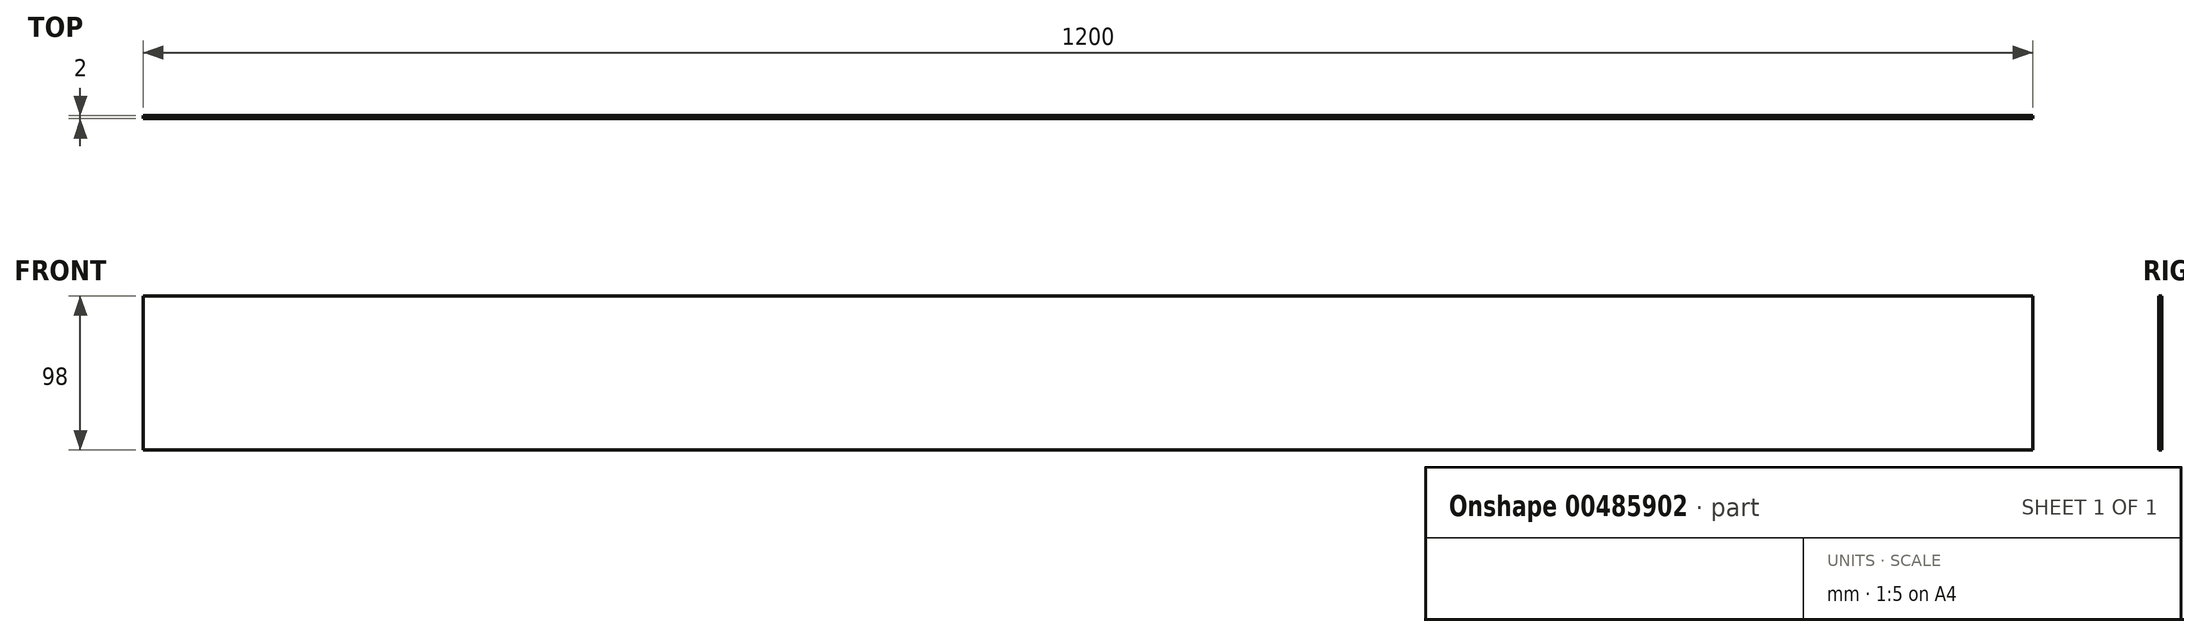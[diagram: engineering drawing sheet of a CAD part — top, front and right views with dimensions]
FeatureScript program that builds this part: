
annotation { "Feature Type Name" : "Feature", "Feature Type Description" : "" }
export const myFeature = defineFeature(function(context is Context, id is Id, definition is map)
    precondition{}
    {
        {
            var Q0;
            Q0=qCreatedBy(makeId("Front.planeOp"),FACE);
            var sketch = newSketch(context, id + "F0", { "sketchPlane" : qUnion([Q0])});
            skLineSegment(sketch, "E0.bottom", {"start": v(600, -49) * mm, "end": v(-600, -49) * mm});
            skLineSegment(sketch, "E0.top", {"start": v(600, 49) * mm, "end": v(-600, 49) * mm});
            skLineSegment(sketch, "E0.left", {"start": v(600, -49) * mm, "end": v(600, 49) * mm});
            skLineSegment(sketch, "E0.right", {"start": v(-600, -49) * mm, "end": v(-600, 49) * mm});
            skPoint(sketch, "E0.middle", {"position": v(0, 0) * mm});
            skSolve(sketch);
        }
        {
            var Q0;
            Q0=qSketchRegion(id+"F0",true);
            extrude(context, id + "F1", {"entities" : qUnion([Q0]), "depth" : 2 * mm});
        }
    });
